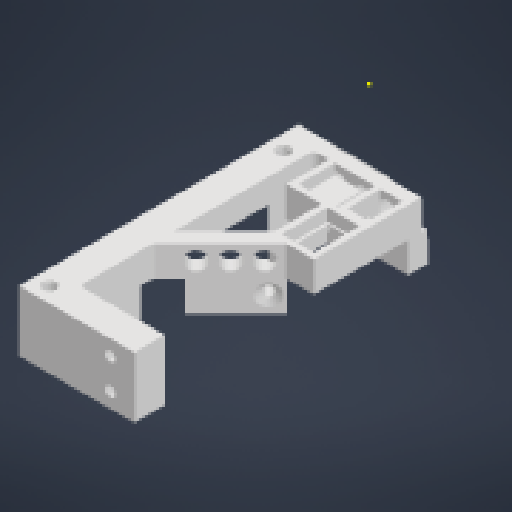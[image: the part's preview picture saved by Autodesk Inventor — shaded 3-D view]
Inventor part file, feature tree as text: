
AUTODESK INVENTOR PART (.ipt)
format: ipt  version: 2023 (Build 270158000, 158)  size: 421,888 bytes
history: native  units: in
note: dims shown in document units (in); Inventor stores cm internally (conversion verified against a paired STEP export)
features: sketch x23, extrude x6, other x3, plane x2, mirror x2
ambient origin geometry x8: Origin, YZ Plane, XZ Plane, XY Plane, X Axis, Y Axis, Z Axis, Center Point
bodies: Solid1 (feature_tree)
feature tree (36):
  other  "mocowanie-czujnika-p.ipt"
  sketch  "Sketch23"  dims[d19=0.4724in]
  extrude  "Extrusion1"  Depth=1.0236in
  extrude  "Extrusion2"  Depth=0.5709in
  extrude  "Extrusion3"  Depth=0.3937in TaperAngle=0.0deg
  extrude  "Extrusion4"  Depth=0.0787in
  extrude  "Extrusion5"  Depth=0.4134in
  plane  "Work Plane1"
  mirror  "Mirror1"
  extrude  "Extrusion6"  TaperAngle=180.0deg  [1 undecoded]
  plane  "Work Plane2"
  mirror  "Mirror2"
  other  "Solid1::mocowanie-czujnika-p.ipt"
  other  "TaggingFeature1"
  sketch  "Sketch1"  dims[d0=0.3937in d1=1.0236in]
  sketch  "Sketch4"  dims[d2=0.5512in d6=0.5709in]
  sketch  "Sketch7"  dims[d10=0.0787in d11=0.0787in]
  sketch  "Sketch8"  dims[d12=0.5906in d13=0.4134in]
  sketch  "Sketch9"  dims[d14=0.0787in d15=180.0deg]
  sketch  "Sketch10"  dims[d16=0.2756in]
  sketch  "Sketch6"  dims[d7=0.6693in d8=0.3937in d9=0.0in]
  sketch  "Sketch12"  dims[d17=0.4331in]
  sketch  "Sketch16"  dims[d18=0.0787in]
  sketch  "Sketch35"  dims[d28=0.1378in]
  sketch  "Sketch36"  dims[d29=0.4724in]
  sketch  "Sketch37"  dims[d30=0.0787in]
  sketch  "Sketch38"  dims[d31=0.3543in d32=0.0in]
  sketch  "Sketch39"  dims[d33=0.1575in]
  sketch  "Sketch41"  dims[d34=0.5906in]
  sketch  "Sketch42"  dims[d35=0.0787in d36=0.0394in d37=0.0in d38=0.0394in d39=0.0276in d40=0.0in]
  sketch  "Sketch24"  dims[d20=0.5118in]
  sketch  "Sketch25"  dims[d21=0.3937in d22=0.0in]
  sketch  "Sketch26"  dims[d23=0.1575in]
  sketch  "Sketch27"  dims[d24=0.1181in]
  sketch  "Sketch28"  dims[d25=0.1575in]
  sketch  "Sketch29"  dims[d26=0.3937in d27=0.0in]
note: 1 required parameter value undecoded (feature->parameter linkage not recoverable at this tier; creation-order binding heuristic only, values carry confidence <= 0.55)
